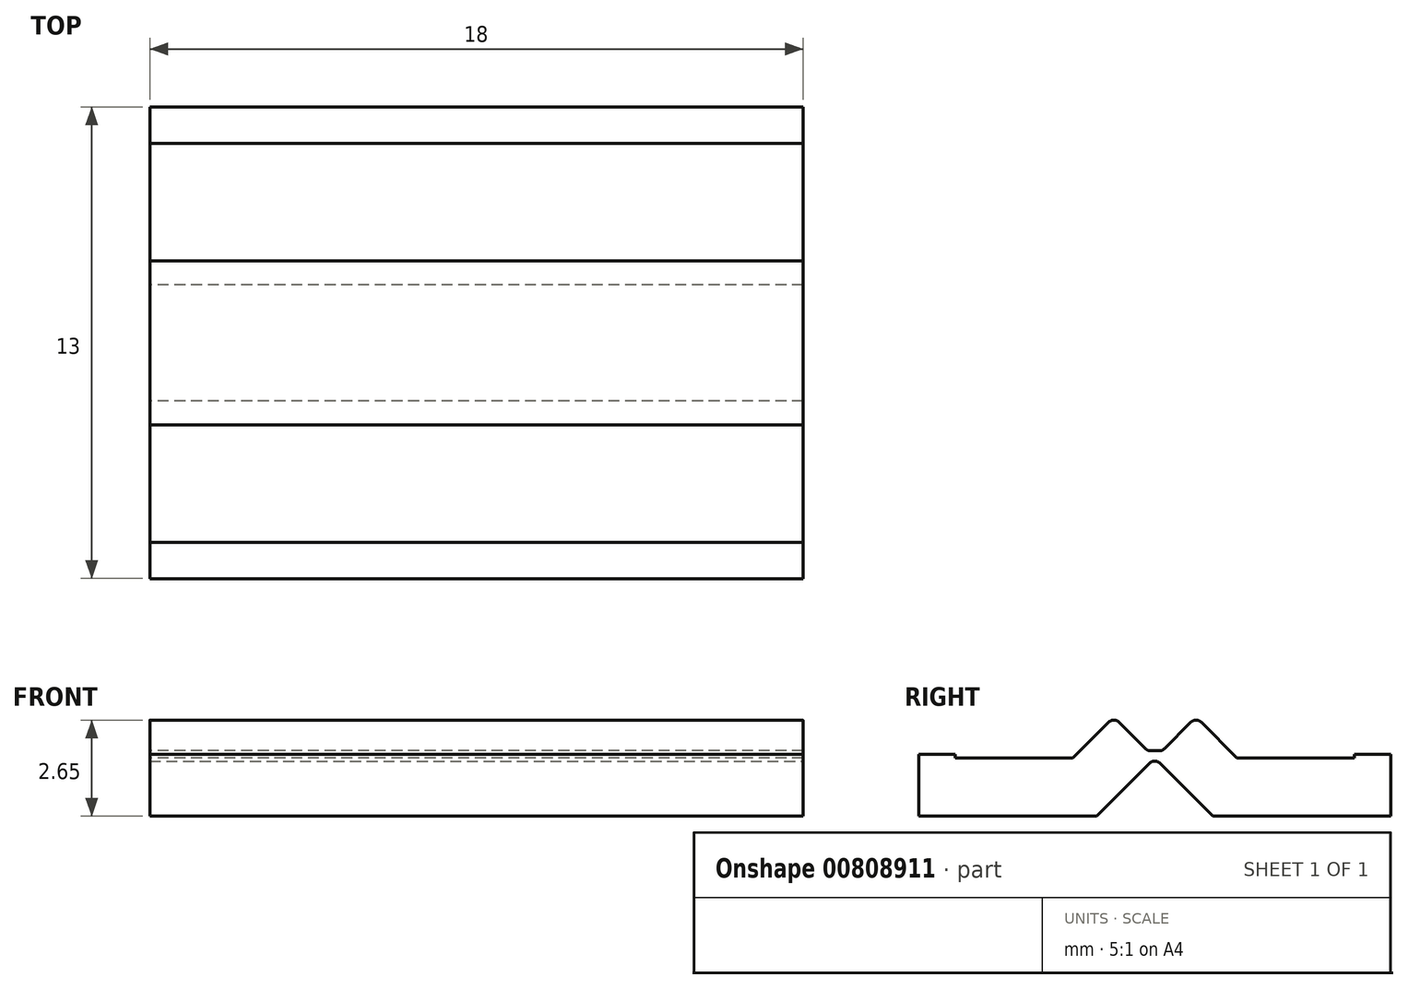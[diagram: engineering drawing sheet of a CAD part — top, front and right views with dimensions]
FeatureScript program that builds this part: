
annotation { "Feature Type Name" : "Feature", "Feature Type Description" : "" }
export const myFeature = defineFeature(function(context is Context, id is Id, definition is map)
    precondition{}
    {
        {
            var Q0;
            Q0=qCreatedBy(makeId("Right.planeOp"),FACE);
            var sketch = newSketch(context, id + "F0", { "sketchPlane" : qUnion([Q0])});
            skLineSegment(sketch, "E0.bottom", {"start": v(-32.25, 0) * mm, "end": v(-27.35, 0) * mm});
            skLineSegment(sketch, "E0.top", {"start": v(-31.25, 1.6) * mm, "end": v(-28.02, 1.6) * mm});
            skLineSegment(sketch, "E0.left", {"start": v(-32.25, 0) * mm, "end": v(-32.25, 1.6) * mm});
            skLineSegment(sketch, "E1.bottom", {"start": v(-27.35, 0) * mm, "end": v(-25.75, 1.6) * mm});
            skLineSegment(sketch, "E1.top", {"start": v(-28.02, 1.6) * mm, "end": v(-26.89, 2.73) * mm});
            skLineSegment(sketch, "E1.right", {"start": v(-25.95, 1.8) * mm, "end": v(-26.89, 2.73) * mm});
            skPoint(sketch, "E2", {"position": v(-28.02, 1.6) * mm});
            skLineSegment(sketch, "E3.top", {"start": v(-32.25, 1.7) * mm, "end": v(-31.25, 1.7) * mm});
            skLineSegment(sketch, "E3.left", {"start": v(-32.25, 1.6) * mm, "end": v(-32.25, 1.7) * mm});
            skLineSegment(sketch, "E3.right", {"start": v(-31.25, 1.6) * mm, "end": v(-31.25, 1.7) * mm});
            skLineSegment(sketch, "E4.top", {"start": v(-25.75, 1.8) * mm, "end": v(-25.95, 1.8) * mm});
            skLineSegment(sketch, "E4.left", {"start": v(-25.75, 1.6) * mm, "end": v(-25.75, 1.8) * mm});
            skSolve(sketch);
        }
        {
            var Q0;
            Q0 = qSketchRegion(id + "F0", true);
            extrude(context, id + "F1", {"entities" : qUnion([Q0]), "depth" : 18 * mm, "offsetDistance" : 25 * mm});
        }
        {
            var Q0;
            Q0=makeQuery(id+"F1.opExtrude","SWEPT_EDGE",EDGE,{"disambiguationData":[OSD([sQuery(id+"F0.wireOp",EDGE,"E1.bottom"),sQuery(id+"F0.wireOp",EDGE,"E4.left")])]});
            cPoint(context, id + "F2", {"entities" : qUnion([Q0]), "parameter" : 0.5});
        }
        {
            var Q0;
            Q0=qCreatedBy(makeId("Front.planeOp"),FACE);
            var Q1;
            Q1 = qCreatedBy(id + "F2" ,VERTEX);
            cPlane(context, id + "F3", {"entities" : qUnion([Q0, Q1]), "cplaneType" : CPlaneType.PLANE_POINT, "offset" : 25 * mm, "width" : 150 * mm, "height" : 150 * mm});
        }
        {
            var Q0;
            Q0=makeQuery(id+"F1.opExtrude","SWEPT_BODY",BODY,{"disambiguationData":[OSD([sQuery(id+"F0.wireOp",EDGE,"E0.bottom"),sQuery(id+"F0.wireOp",EDGE,"E0.top"),sQuery(id+"F0.wireOp",EDGE,"E0.left"),sQuery(id+"F0.wireOp",EDGE,"E1.bottom"),sQuery(id+"F0.wireOp",EDGE,"E1.top"),sQuery(id+"F0.wireOp",EDGE,"E1.right"),sQuery(id+"F0.wireOp",EDGE,"E3.top"),sQuery(id+"F0.wireOp",EDGE,"E3.left"),sQuery(id+"F0.wireOp",EDGE,"E3.right")])]});
            var Q1;
            Q1=qCreatedBy(id+"F3.planeOp",FACE);
            mirror(context, id + "F4", {"operationType" : NewBodyOperationType.ADD, "entities" : qUnion([Q0]), "mirrorPlane" : qUnion([Q1])});
        }
        {
            var Q0;
            Q0=makeQuery(id+"F4.opPattern","COPY",EDGE,{"derivedFrom":makeQuery(id+"F1.opExtrude","SWEPT_EDGE",EDGE,{"disambiguationData":[OSD([sQuery(id+"F0.wireOp",EDGE,"E1.right"),sQuery(id+"F0.wireOp",EDGE,"E4.top")])]}),"instanceName":"1"});
            var Q1;
            Q1=makeQuery(id+"F1.opExtrude","SWEPT_EDGE",EDGE,{"disambiguationData":[OSD([sQuery(id+"F0.wireOp",EDGE,"E1.right"),sQuery(id+"F0.wireOp",EDGE,"E4.top")])]});
            var Q2;
            {var subQ0=makeQuery(id+"F1.opExtrude","SWEPT_EDGE",EDGE,{"disambiguationData":[OSD([sQuery(id+"F0.wireOp",EDGE,"E1.bottom"),sQuery(id+"F0.wireOp",EDGE,"E4.left")])]});Q2=makeQuery(id+"F4.boolean.opBoolean","MERGE",EDGE,{"derivedFrom":[subQ0,makeQuery(id+"F4.opPattern","COPY",EDGE,{"derivedFrom":subQ0,"instanceName":"1"})]});}
            var Q3;
            Q3=makeQuery(id+"F4.opPattern","COPY",EDGE,{"derivedFrom":makeQuery(id+"F1.opExtrude","SWEPT_EDGE",EDGE,{"disambiguationData":[OSD([sQuery(id+"F0.wireOp",EDGE,"E1.top"),sQuery(id+"F0.wireOp",EDGE,"E1.right")])]}),"instanceName":"1"});
            var Q4;
            Q4=makeQuery(id+"F1.opExtrude","SWEPT_EDGE",EDGE,{"disambiguationData":[OSD([sQuery(id+"F0.wireOp",EDGE,"E1.top"),sQuery(id+"F0.wireOp",EDGE,"E1.right")])]});
            fillet(context, id + "F5", {"entities" : qUnion([Q0, Q1, Q2, Q3, Q4]), "radius" : 0.2 * mm, "allowEdgeOverflow" : false});
        }
    });
